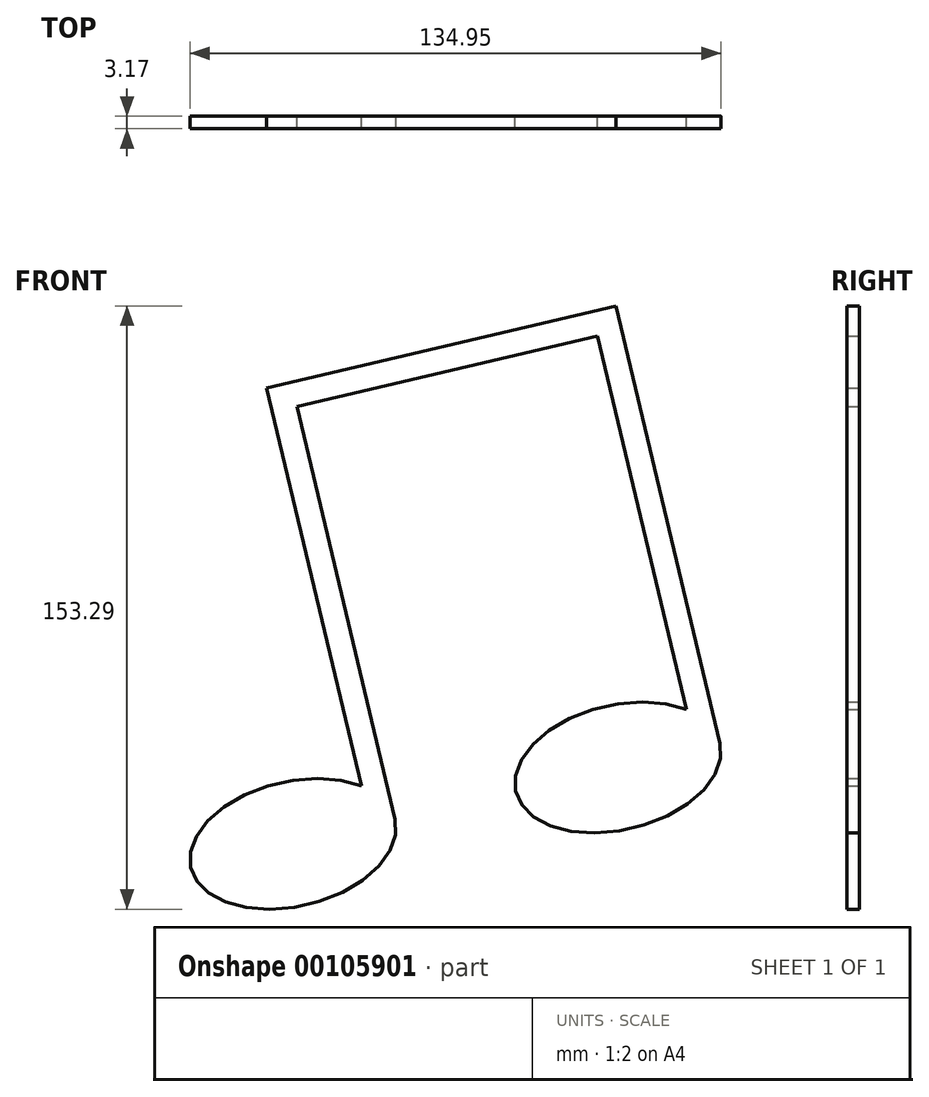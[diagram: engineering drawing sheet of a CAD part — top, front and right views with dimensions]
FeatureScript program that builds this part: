
annotation { "Feature Type Name" : "Feature", "Feature Type Description" : "" }
export const myFeature = defineFeature(function(context is Context, id is Id, definition is map)
    precondition{}
    {
        {
            var Q0;
            Q0=qCreatedBy(makeId("Front.planeOp"),FACE);
            var sketch = newSketch(context, id + "F0", { "sketchPlane" : qUnion([Q0])});
            skEllipticalArc(sketch, "E0", {});
            skLineSegment(sketch, "E1", {"start": v(-6.7, 115.84) * mm, "end": v(17.39, 14.7) * mm});
            skEllipticalArc(sketch, "E2", {});
            skLineSegment(sketch, "E3", {"start": v(108.5, 25.56) * mm, "end": v(82.04, 136.66) * mm});
            skLineSegment(sketch, "E4", {"start": v(-6.7, 115.84) * mm, "end": v(82.04, 136.66) * mm});
            skLineSegment(sketch, "E5", {"start": v(25.94, 6.18) * mm, "end": v(0.96, 111.1) * mm});
            skLineSegment(sketch, "E6", {"start": v(0.96, 111.1) * mm, "end": v(77.33, 129.04) * mm});
            skLineSegment(sketch, "E7", {"start": v(77.33, 129.04) * mm, "end": v(99.94, 34.09) * mm});
            const initialGuessF0  = {"E0": [0, 0, -0.9728012308245748, -0.23164145852198462, 0.02667, 0.015875, 3.8461400720426373, 3.1415926535897927], "E2": [0.08255, 0.01937778668326974, -0.9728012308245747, -0.23164145852198514, 0.02667, 0.015875, 3.846140072042637, 3.141592653589793]};
            skSetInitialGuess(sketch, initialGuessF0);
            skSolve(sketch);
        }
        {
            var Q0;
            Q0=qSketchRegion(id+"F0",true);
            extrude(context, id + "F1", {"entities" : qUnion([Q0]), "depth" : 3.17 * mm});
        }
    });
